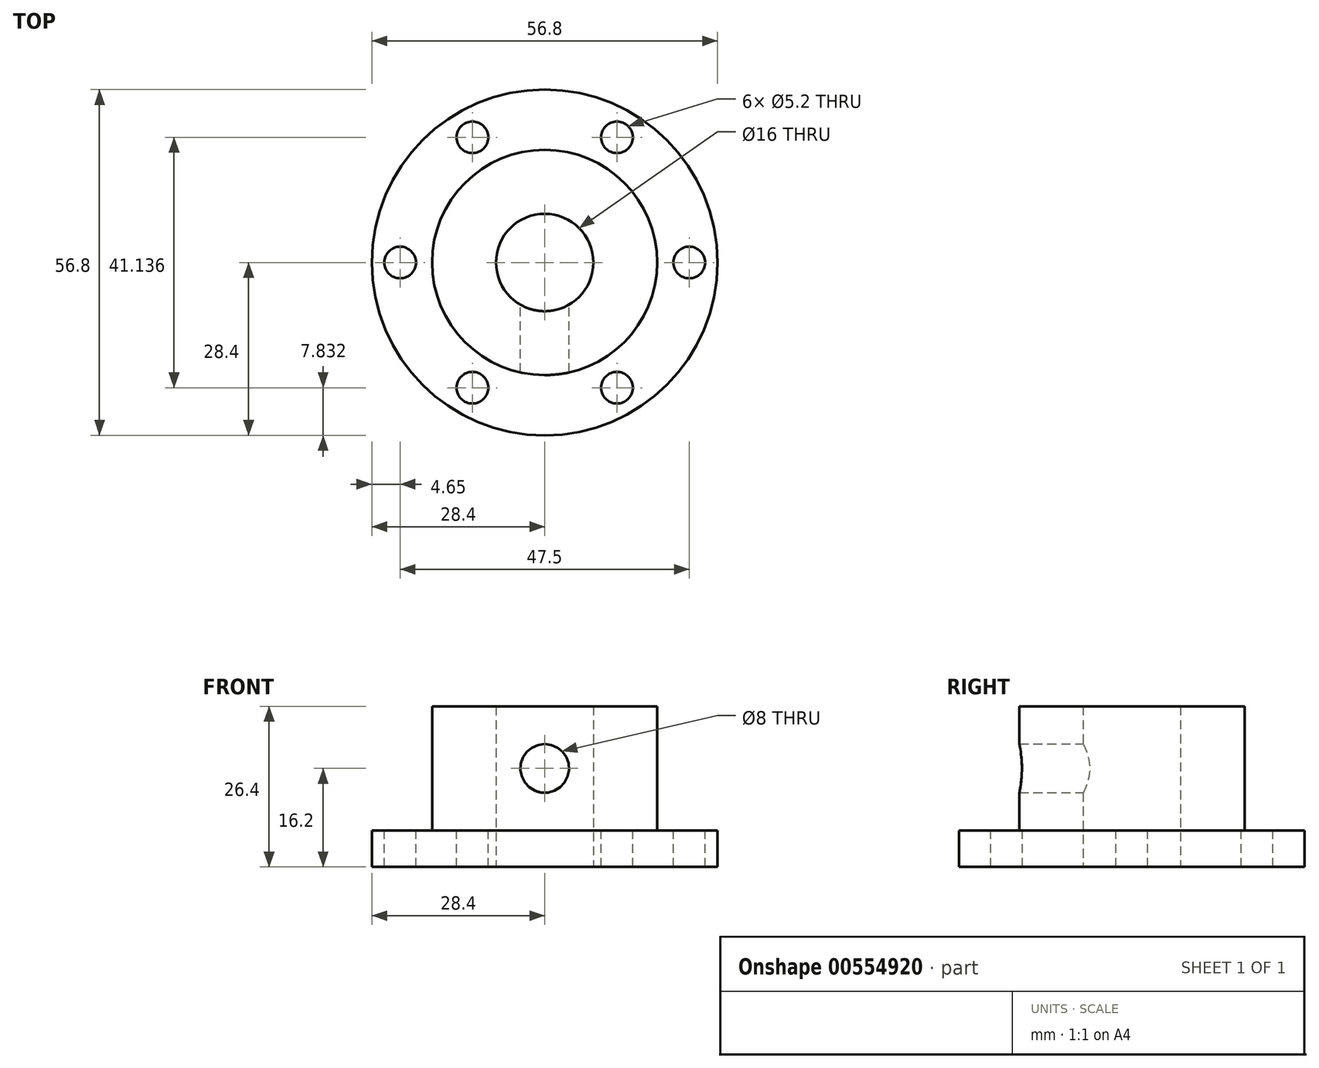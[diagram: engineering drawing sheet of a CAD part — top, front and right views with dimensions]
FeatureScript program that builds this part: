
annotation { "Feature Type Name" : "Feature", "Feature Type Description" : "" }
export const myFeature = defineFeature(function(context is Context, id is Id, definition is map)
    precondition{}
    {
        {
            var Q0;
            Q0=qCreatedBy(makeId("Front.planeOp"),FACE);
            var sketch = newSketch(context, id + "F0", { "sketchPlane" : qUnion([Q0])});
            skLineSegment(sketch, "E0", {"start": v(-8, 0) * mm, "end": v(-28.4, 0) * mm});
            skLineSegment(sketch, "E1", {"start": v(-28.4, 0) * mm, "end": v(-28.4, 6) * mm});
            skLineSegment(sketch, "E2", {"start": v(-28.4, 6) * mm, "end": v(-18.5, 6) * mm});
            skLineSegment(sketch, "E3", {"start": v(-18.5, 6) * mm, "end": v(-18.5, 26.4) * mm});
            skLineSegment(sketch, "E4", {"start": v(-18.5, 26.4) * mm, "end": v(-8, 26.4) * mm});
            skLineSegment(sketch, "E5", {"start": v(-8, 26.4) * mm, "end": v(-8, 0) * mm});
            skLineSegment(sketch, "E6", {"start": v(0, 0) * mm, "end": v(0, 43.03) * mm, "construction": true});
            skSolve(sketch);
        }
        {
            var Q0;
            Q0=qSketchRegion(id+"F0",true);
            var Q1;
            Q1=sQuery(id+"F0.wireOp",EDGE,"E6");
            revolve(context, id + "F1", {"entities" : qUnion([Q0]), "axis" : qUnion([Q1]), "revolveType" : RevolveType.FULL});
        }
        {
            var Q0;
            Q0=makeQuery(id+"F1.opRevolve","SWEPT_FACE",FACE,{"disambiguationData":[OSD([sQuery(id+"F0.wireOp",EDGE,"E2")])]});
            var sketch = newSketch(context, id + "F2", { "sketchPlane" : qUnion([Q0])});
            skCircle(sketch, "E7", {"center": v(0, 0) * mm, "radius": 23.75 * mm, "construction": true});
            skCircle(sketch, "E8", {"center": v(-23.75, 0) * mm, "radius": 2.6 * mm});
            skCircle(sketch, "E9.1.0", {"center": v(-11.88, -20.57) * mm, "radius": 2.6 * mm});
            skCircle(sketch, "E9.2.0", {"center": v(11.87, -20.57) * mm, "radius": 2.6 * mm});
            skCircle(sketch, "E9.3.0", {"center": v(23.75, 0) * mm, "radius": 2.6 * mm});
            skCircle(sketch, "E9.4.0", {"center": v(11.88, 20.57) * mm, "radius": 2.6 * mm});
            skCircle(sketch, "E9.5.0", {"center": v(-11.88, 20.57) * mm, "radius": 2.6 * mm});
            skSolve(sketch);
        }
        {
            var Q0;
            Q0=qSketchRegion(id+"F2",true);
            extrude(context, id + "F3", {"entities" : qUnion([Q0]), "operationType" : NewBodyOperationType.REMOVE, "endBound" : BoundingType.THROUGH_ALL, "oppositeDirection" : true, "depth" : 25 * mm, "offsetDistance" : 25 * mm});
        }
        {
            var Q0;
            Q0=qCreatedBy(makeId("Front.planeOp"),FACE);
            var sketch = newSketch(context, id + "F4", { "sketchPlane" : qUnion([Q0])});
            skLineSegment(sketch, "E10", {"start": v(0, 0) * mm, "end": v(0, 16.2) * mm, "construction": true});
            skCircle(sketch, "E11", {"center": v(0, 16.2) * mm, "radius": 4 * mm});
            skSolve(sketch);
        }
        {
            var Q0;
            Q0=qSketchRegion(id+"F4",true);
            extrude(context, id + "F5", {"entities" : qUnion([Q0]), "operationType" : NewBodyOperationType.REMOVE, "depth" : 25 * mm, "offsetDistance" : 25 * mm});
        }
    });
